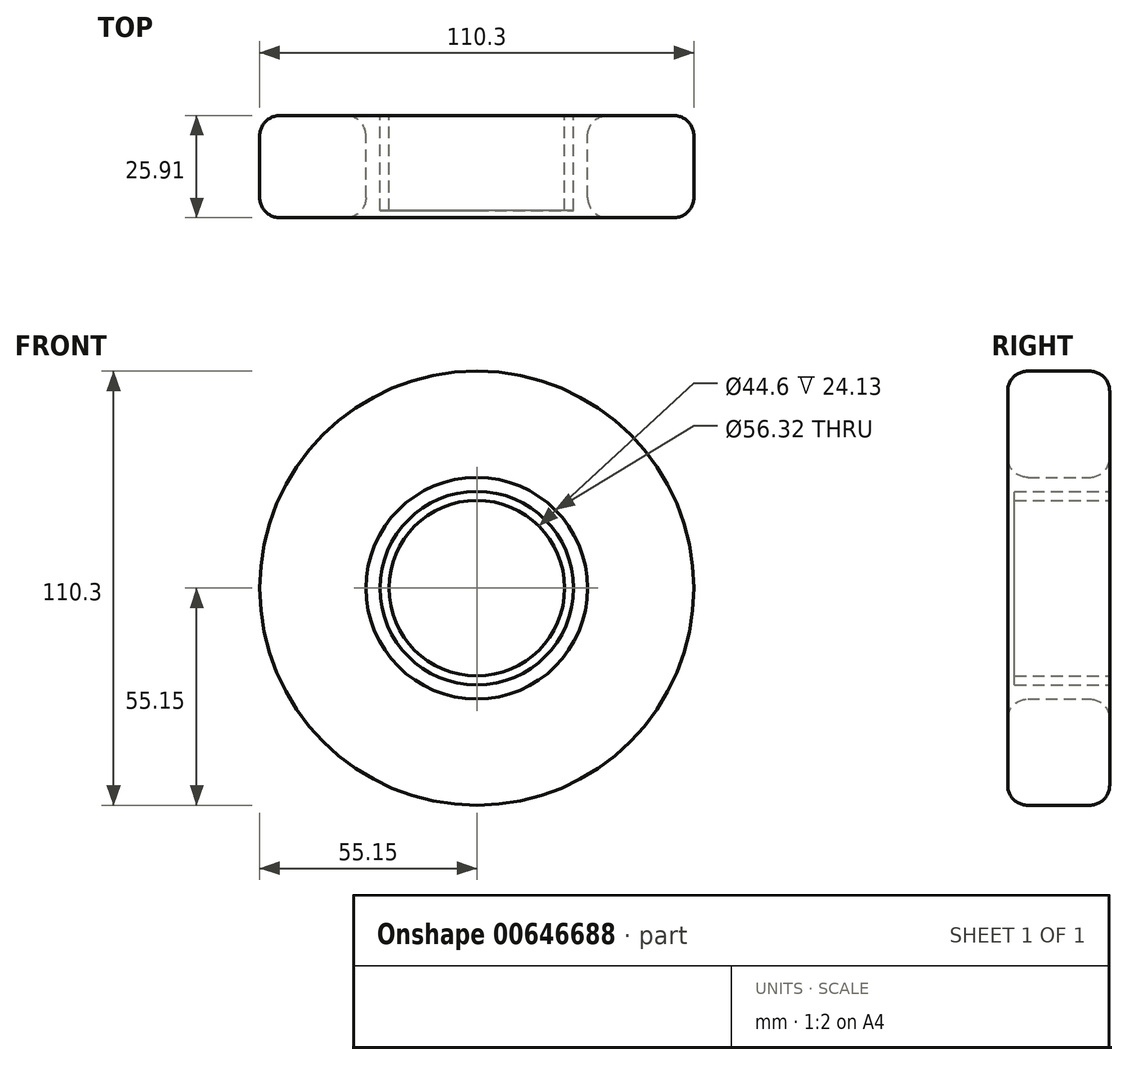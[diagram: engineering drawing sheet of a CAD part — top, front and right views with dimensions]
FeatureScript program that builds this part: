
annotation { "Feature Type Name" : "Feature", "Feature Type Description" : "" }
export const myFeature = defineFeature(function(context is Context, id is Id, definition is map)
    precondition{}
    {
        {
            var Q0;
            Q0=qCreatedBy(makeId("Front.planeOp"),FACE);
            var sketch = newSketch(context, id + "F0", { "sketchPlane" : qUnion([Q0])});
            skCircle(sketch, "E0", {"center": v(0, 0) * mm, "radius": 55.15 * mm});
            skCircle(sketch, "E1", {"center": v(0, 0) * mm, "radius": 28.16 * mm});
            skSolve(sketch);
        }
        {
            var Q0;
            Q0=makeQuery(id+"F0.imprint","IMPRINT",FACE,{"disambiguationData":[TD([[makeQuery(id+"F0.imprint","IMPRINT",EDGE,{"derivedFrom":sQuery(id+"F0.wireOp",EDGE,"E0")}),1.0]])]});
            extrude(context, id + "F1", {"entities" : qUnion([Q0]), "depth" : 25.9 * mm, "offsetDistance" : 25.4 * mm});
        }
        {
            var Q0;
            Q0=makeQuery(id+"F1.opExtrude","CAP_EDGE",EDGE,{"disambiguationData":[OSD([sQuery(id+"F0.wireOp",EDGE,"E1")])],"isStart":false});
            var Q1;
            Q1=makeQuery(id+"F1.opExtrude","CAP_EDGE",EDGE,{"disambiguationData":[OSD([sQuery(id+"F0.wireOp",EDGE,"E0")])],"isStart":false});
            var Q2;
            Q2=makeQuery(id+"F1.opExtrude","CAP_EDGE",EDGE,{"disambiguationData":[OSD([sQuery(id+"F0.wireOp",EDGE,"E0")])],"isStart":true});
            var Q3;
            Q3=makeQuery(id+"F1.opExtrude","CAP_EDGE",EDGE,{"disambiguationData":[OSD([sQuery(id+"F0.wireOp",EDGE,"E1")])],"isStart":true});
            fillet(context, id + "F2", {"entities" : qUnion([Q0, Q1, Q2, Q3]), "radius" : 5.08 * mm, "tangentPropagation" : true, "allowEdgeOverflow" : false});
        }
        {
            var Q0;
            Q0=qCreatedBy(makeId("Front.planeOp"),FACE);
            var sketch = newSketch(context, id + "F3", { "sketchPlane" : qUnion([Q0])});
            skCircle(sketch, "E2", {"center": v(0, 0) * mm, "radius": 24.6 * mm});
            skCircle(sketch, "E3", {"center": v(0, 0) * mm, "radius": 22.3 * mm});
            skSolve(sketch);
        }
        {
            var Q0;
            Q0=makeQuery(id+"F3.imprint","IMPRINT",FACE,{"disambiguationData":[TD([[makeQuery(id+"F3.imprint","IMPRINT",EDGE,{"derivedFrom":sQuery(id+"F3.wireOp",EDGE,"E2")}),1.0]])]});
            extrude(context, id + "F4", {"entities" : qUnion([Q0]), "depth" : 24.13 * mm, "offsetDistance" : 25.4 * mm});
        }
    });
